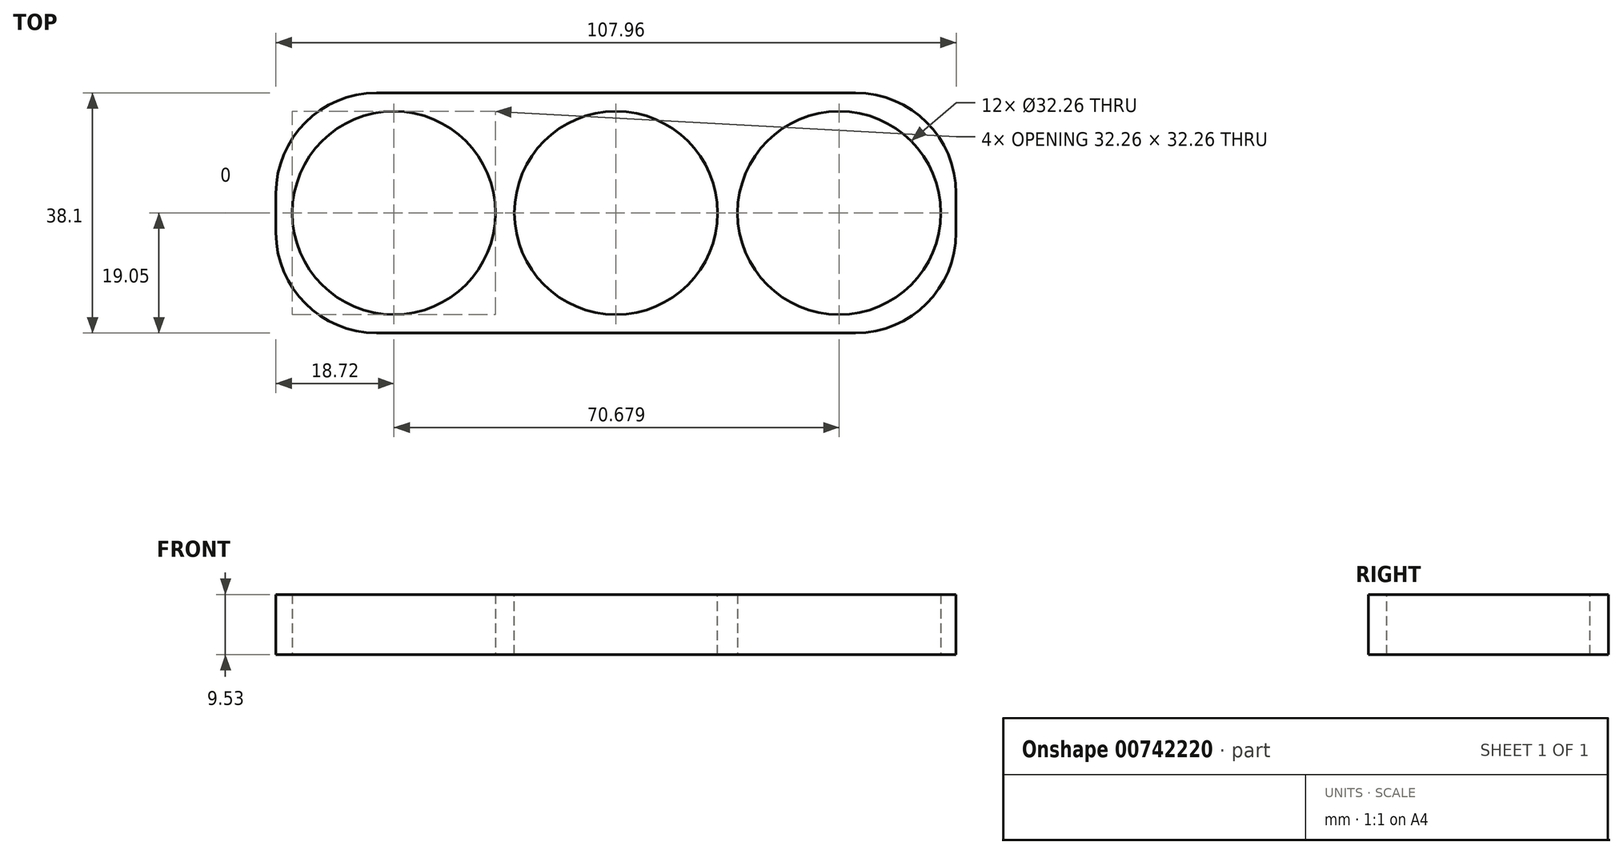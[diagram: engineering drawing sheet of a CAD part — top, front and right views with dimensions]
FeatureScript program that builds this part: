
annotation { "Feature Type Name" : "Feature", "Feature Type Description" : "" }
export const myFeature = defineFeature(function(context is Context, id is Id, definition is map)
    precondition{}
    {
        {
            var Q0;
            Q0=qCreatedBy(makeId("Top.planeOp"),FACE);
            var sketch = newSketch(context, id + "F0", { "sketchPlane" : qUnion([Q0])});
            skLineSegment(sketch, "E0.bottom", {"start": v(53.98, -19.05) * mm, "end": v(-53.97, -19.05) * mm});
            skLineSegment(sketch, "E0.top", {"start": v(53.97, 19.05) * mm, "end": v(-53.98, 19.05) * mm});
            skLineSegment(sketch, "E0.left", {"start": v(53.98, -19.05) * mm, "end": v(53.98, 19.05) * mm});
            skLineSegment(sketch, "E0.right", {"start": v(-53.97, -19.05) * mm, "end": v(-53.98, 19.05) * mm});
            skPoint(sketch, "E0.middle", {"position": v(0, 0) * mm});
            skSolve(sketch);
        }
        {
            var Q0;
            Q0 = qSketchRegion(id + "F0", true);
            extrude(context, id + "F1", {"entities" : qUnion([Q0]), "depth" : 9.52 * mm, "offsetDistance" : 25.4 * mm});
        }
        {
            var Q0;
            Q0=makeQuery(id+"F1.opExtrude","CAP_FACE",FACE,{"disambiguationData":[OSD([sQuery(id+"F0.wireOp",EDGE,"E0.bottom"),sQuery(id+"F0.wireOp",EDGE,"E0.top"),sQuery(id+"F0.wireOp",EDGE,"E0.left"),sQuery(id+"F0.wireOp",EDGE,"E0.right")])],"isStart":false});
            var sketch = newSketch(context, id + "F2", { "sketchPlane" : qUnion([Q0])});
            skCircle(sketch, "E1", {"center": v(0, 0) * mm, "radius": 15.88 * mm});
            skSolve(sketch);
        }
        {
            var Q0;
            Q0=sQuery(id+"F2.wireOp",VERTEX,"E1.center");
            var Q1;
            Q1=makeQuery(id+"F1.opExtrude","SWEPT_BODY",BODY,{"disambiguationData":[OSD([sQuery(id+"F0.wireOp",EDGE,"E0.bottom"),sQuery(id+"F0.wireOp",EDGE,"E0.top"),sQuery(id+"F0.wireOp",EDGE,"E0.left"),sQuery(id+"F0.wireOp",EDGE,"E0.right")])]});
            hole(context, id + "F3", {"style" : HoleStyle.SIMPLE, "endStyle" : HoleEndStyle.THROUGH, "holeDiameter" : 32.26 * mm, "majorDiameter" : 6.35 * mm, "isTappedThrough" : true, "tappedDepth" : 12.7 * mm, "tapClearance" : 3, "locations" : qUnion([Q0]), "scope" : qUnion([Q1])});
        }
        {
            var Q0;
            Q0=qCreatedBy(makeId("Top.planeOp"),FACE);
            var sketch = newSketch(context, id + "F4", { "sketchPlane" : qUnion([Q0])});
            skCircle(sketch, "E2.0", {"center": v(0, 0) * mm, "radius": 16.13 * mm});
            skCircle(sketch, "E3", {"center": v(-35.26, 0) * mm, "radius": 15.88 * mm});
            skCircle(sketch, "E4", {"center": v(35.2, -0.14) * mm, "radius": 15.88 * mm});
            skSolve(sketch);
        }
        {
            var Q0;
            Q0=sQuery(id+"F4.wireOp",VERTEX,"E3.center");
            var Q1;
            Q1=makeQuery(id+"F1.opExtrude","SWEPT_BODY",BODY,{"disambiguationData":[OSD([sQuery(id+"F0.wireOp",EDGE,"E0.bottom"),sQuery(id+"F0.wireOp",EDGE,"E0.top"),sQuery(id+"F0.wireOp",EDGE,"E0.left"),sQuery(id+"F0.wireOp",EDGE,"E0.right")])]});
            hole(context, id + "F5", {"style" : HoleStyle.SIMPLE, "endStyle" : HoleEndStyle.THROUGH, "oppositeDirection" : true, "holeDiameter" : 32.26 * mm, "majorDiameter" : 6.35 * mm, "isTappedThrough" : true, "tappedDepth" : 12.7 * mm, "tapClearance" : 3, "locations" : qUnion([Q0]), "scope" : qUnion([Q1])});
        }
        {
            var Q0;
            Q0=qCreatedBy(makeId("Top.planeOp"),FACE);
            var sketch = newSketch(context, id + "F6", { "sketchPlane" : qUnion([Q0])});
            skCircle(sketch, "E5", {"center": v(35.42, 0) * mm, "radius": 15.88 * mm});
            skSolve(sketch);
        }
        {
            var Q0;
            Q0=sQuery(id+"F6.wireOp",VERTEX,"E5.center");
            var Q1;
            Q1=makeQuery(id+"F1.opExtrude","SWEPT_BODY",BODY,{"disambiguationData":[OSD([sQuery(id+"F0.wireOp",EDGE,"E0.bottom"),sQuery(id+"F0.wireOp",EDGE,"E0.top"),sQuery(id+"F0.wireOp",EDGE,"E0.left"),sQuery(id+"F0.wireOp",EDGE,"E0.right")])]});
            hole(context, id + "F7", {"style" : HoleStyle.SIMPLE, "endStyle" : HoleEndStyle.THROUGH, "oppositeDirection" : true, "holeDiameter" : 32.26 * mm, "majorDiameter" : 6.35 * mm, "isTappedThrough" : true, "tappedDepth" : 12.7 * mm, "tapClearance" : 3, "locations" : qUnion([Q0]), "scope" : qUnion([Q1])});
        }
        {
            var Q0;
            Q0=makeQuery(id+"F1.opExtrude","SWEPT_EDGE",EDGE,{"disambiguationData":[OSD([sQuery(id+"F0.wireOp",EDGE,"E0.top"),sQuery(id+"F0.wireOp",EDGE,"E0.left")])]});
            fillet(context, id + "F8", {"entities" : qUnion([Q0]), "radius" : 15.94 * mm, "tangentPropagation" : true, "allowEdgeOverflow" : false});
        }
        {
            var Q0;
            Q0=makeQuery(id+"F1.opExtrude","SWEPT_EDGE",EDGE,{"disambiguationData":[OSD([sQuery(id+"F0.wireOp",EDGE,"E0.bottom"),sQuery(id+"F0.wireOp",EDGE,"E0.left")])]});
            fillet(context, id + "F9", {"entities" : qUnion([Q0]), "radius" : 15.95 * mm, "tangentPropagation" : true, "allowEdgeOverflow" : false});
        }
        {
            var Q0;
            Q0=makeQuery(id+"F1.opExtrude","SWEPT_EDGE",EDGE,{"disambiguationData":[OSD([sQuery(id+"F0.wireOp",EDGE,"E0.bottom"),sQuery(id+"F0.wireOp",EDGE,"E0.right")])]});
            fillet(context, id + "F10", {"entities" : qUnion([Q0]), "radius" : 15.95 * mm, "tangentPropagation" : true, "allowEdgeOverflow" : false});
        }
        {
            var Q0;
            Q0=makeQuery(id+"F1.opExtrude","SWEPT_EDGE",EDGE,{"disambiguationData":[OSD([sQuery(id+"F0.wireOp",EDGE,"E0.top"),sQuery(id+"F0.wireOp",EDGE,"E0.right")])]});
            fillet(context, id + "F11", {"entities" : qUnion([Q0]), "radius" : 15.95 * mm, "tangentPropagation" : true, "allowEdgeOverflow" : false});
        }
    });
